# Revit family: Forniture_Tables_Plank_MisterX_ table Square  h50
name_source: partatom
category: Furniture
revit_build: Autodesk Revit 2017 (Build: 20160225_1515(x64)
units: mm (PartAtom-declared; Revit-internal decimal feet)

## family parameters
Cut with Voids When Loaded = No
Host = Face
Room Calculation Point = No
Shared = No

## types (2) — shared parameters
Anti-slip rubber = Plank - Anti-slip rubber
BIMobject category = Tables
BIMobject category code = furniture-tables
BIMobject main category = Furniture
BIMobject main category code = furniture
Brand url = http://www.plank.it
Data sheet = https://www.plank.it
Default Elevation = 1219 mm
Description = Table. Four star cast iron base black or white powder coated.
Table top in high pressure laminate (HPL) Full Color or in
MDF powder coated in black or white.
Design country = Italy
Edition number = 1
Four - spoke base = Plank - Powder coated cast iron
IFC Classification = Furnishing Element
Manufacturer = Plank S.r.l.  - Ora (BZ)
Manufacturer country = Italy
Manufacturer name = PLANK
Masterformat 2014 Code = 12 00 00
Masterformat 2014 Description = Furnishings
Material main = Cast iron
Material secondary = MDF
NBS Reference Code = 31
NBS Reference Description = Fittings, Furnishings And Equipment (Ff&E) Products
Nominal height = 500 mm  [stored 1.64042 ft]
Nominal width = 680 mm  [stored 2.23097 ft]
OmniClass Code = 23-21 00 00
OmniClass Description = Furnishings, Fixtures and Equipment Products
Product Guid = bf6ef074-8844-44a0-90f9-36f74eede1cf
Product SKU = MisterX-table-Square-h-50
Product data url = https://bimobject.com
Product family = MisterX
Product group = Table
Product url = https://www.plank.it
QR code = http://bimobject.com
Shape = Square
Table Top = Plank - MDF varnished
Technical description = https://www.plank.it
Type = Forniture
UNSPSC Code = 56
URL = https://www.plank.it
Uniclass 1.4 Code = JN
Uniclass 1.4 Description = Furniture/Equipment
Uniclass 2.0 Code = EE-35
Uniclass 2.0 Description = Fittings, Furnishings And Equipment (Ff&E) And Signage Elements
Uniclass 2015 Code = EF_40_30
Uniclass 2015 Name = Furnishings
Uniformat II Code = E2020
Uniformat II Description = Movable Furnishings
Weight Net (Kg) = 0

## per-type parameters (varying)
| type | Side length A | Side length B |
| MISTER_ X 9510-51 (70x70 cm) | 350 mm  [stored 1.14829 ft] | 350 mm  [stored 1.14829 ft] |
| MISTER_ X 9511-51 (80x80 cm) | 400 mm  [stored 1.31234 ft] | 400 mm  [stored 1.31234 ft] |

note: column(s) folded — value = type name in every type: Model

note: [stored X ft] marks values corroborated as IEEE doubles in the binary element streams (Revit-internal decimal feet)
